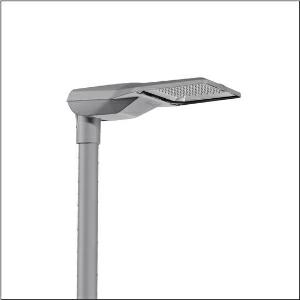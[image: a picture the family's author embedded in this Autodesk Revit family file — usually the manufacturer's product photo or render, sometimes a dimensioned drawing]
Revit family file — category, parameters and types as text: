
# Revit family: streetlight_sl_21_iq_midi___pc-l_5xe3f41g08mb_febf
name_source: partatom
category: Lighting Fixtures
units: mm (PartAtom-declared; Revit-internal decimal feet)

## family parameters
Cut with Voids When Loaded = No
Host = Face
Light Source = No
Part Type = Normal
Room Calculation Point = No
Round Connector Dimension = Use Diameter
Shared = No

## types (1)
- --- (1 x LED, 19370 lm, 146.7 W, 4000K)
    Apparent Load = 147 VA
    CIE Flux Codes = 38 78 98 100 100
    Color Rendering = 70
    Color Temperature = 4000K
    Default Elevation = 1800 mm
    Description = Streetlight SL 21 iQ midi, mast luminaire, primary light control with lens, of PMMA, primary optical cover: cover, of toughened safety glass, transparent, light distribution: PC-L, light emission: direct distribution, primary light characteristic: asymmetric, left, installation type: post-top, side-entry, LED, High Power LED, rated luminous flux: 19.370lm, luminous efficacy: 132lm/W, light colour: 740, colour temperature: 4000K, control: Street-Remote, Auto-Match, Temp-Guard, Lumen-Switch, Night-Set, Smart-Wire, Light-Fading, Desk-Remote (wireless, voltage-free reading and setting of iQ features in the workshop via application-optimized NFC function/RFID function), optimised constant luminous flux control (CLO 2.0), presetting dimming linear, mains connection: 230..240V, AC, 50/60Hz, start of lifetime: 147W, end of service life: 161W, reduction: 62W, luminaire housing, of diecast aluminium, powder-coated, Siteco® metallic grey (DB 702S), corrosivity category C5 mid according to DIN EN ISO 12944, please order mast flange separately, inclination adjustable: 0°, 5°, 10°, 15°, sealing non-destructively replaceable, multi-level sealing system, length: 644mm, width: 335mm, height: 110mm, mast flange for spigot size: 42mm (side-entry): 5XC10008XM4, 60/48mm (side-entry/post-top): 5XC10108XM2, 76/60mm (side-entry/post-top): 5XC10108XM1, protection rating (complete): IP66, insulation class (complete): insulation class II (safety insulation), certification: CE, ENEC, ENEC+, VDE, impact resistance: IK09, permissible operating ambient temperature for outdoor applications: -40..+50°C, standard-compliant lighting for roads and squares, packaging unit: 1 piece

Light Distribution: PC-L
    Height = 111 mm
    Lamp = 1 x LED
    Lamp Light Flux = 19370 lm
    Lamp Power = 146.7 W
    Lamp count = 1
    Length = 644 mm
    Luminous efficacy = 132 lm/W
    Manufacturer = Siteco
    ModVariant = No
    Model = 5XE3F41G08MB
    Number of Poles = 1
    OnlyDefault = Yes
    Power Factor = 1
    Product Name = Streetlight SL 21 iQ midi | PC-L
    Product group = mast luminaire | pylon top
    ProductGroupID = 6100
    Protection Class = Protection class II
    Protection Degree = IP 66
    RLX_Detail_Level = 1
    RLX_Emergency_Light_Flux = 0 lm
    RLX_Emergency_Type = 0
    RLX_Emergency_Type_DB = No
    RlxData = <blob elided: 93769 chars, md5=c3413754>
    Socket = socket
    Standby Power = 0 W
    System Light Flux = 19370 lm
    System Power = 147 W
    Type Comments = factory setting: luminous flux: 100 % | dim-lin: 254 | 753 mA
    Type Image = l_1004298.jpg
    URL = http://relux.com
    VarID = @adj_005447
    Voltage = 0 V
    Weight = 0.00 kg
    Width = 336 mm

## geometry (parser evidence)
native form markers: Blend x4, Sweep x10
no freeform markers — native parametric forms only
